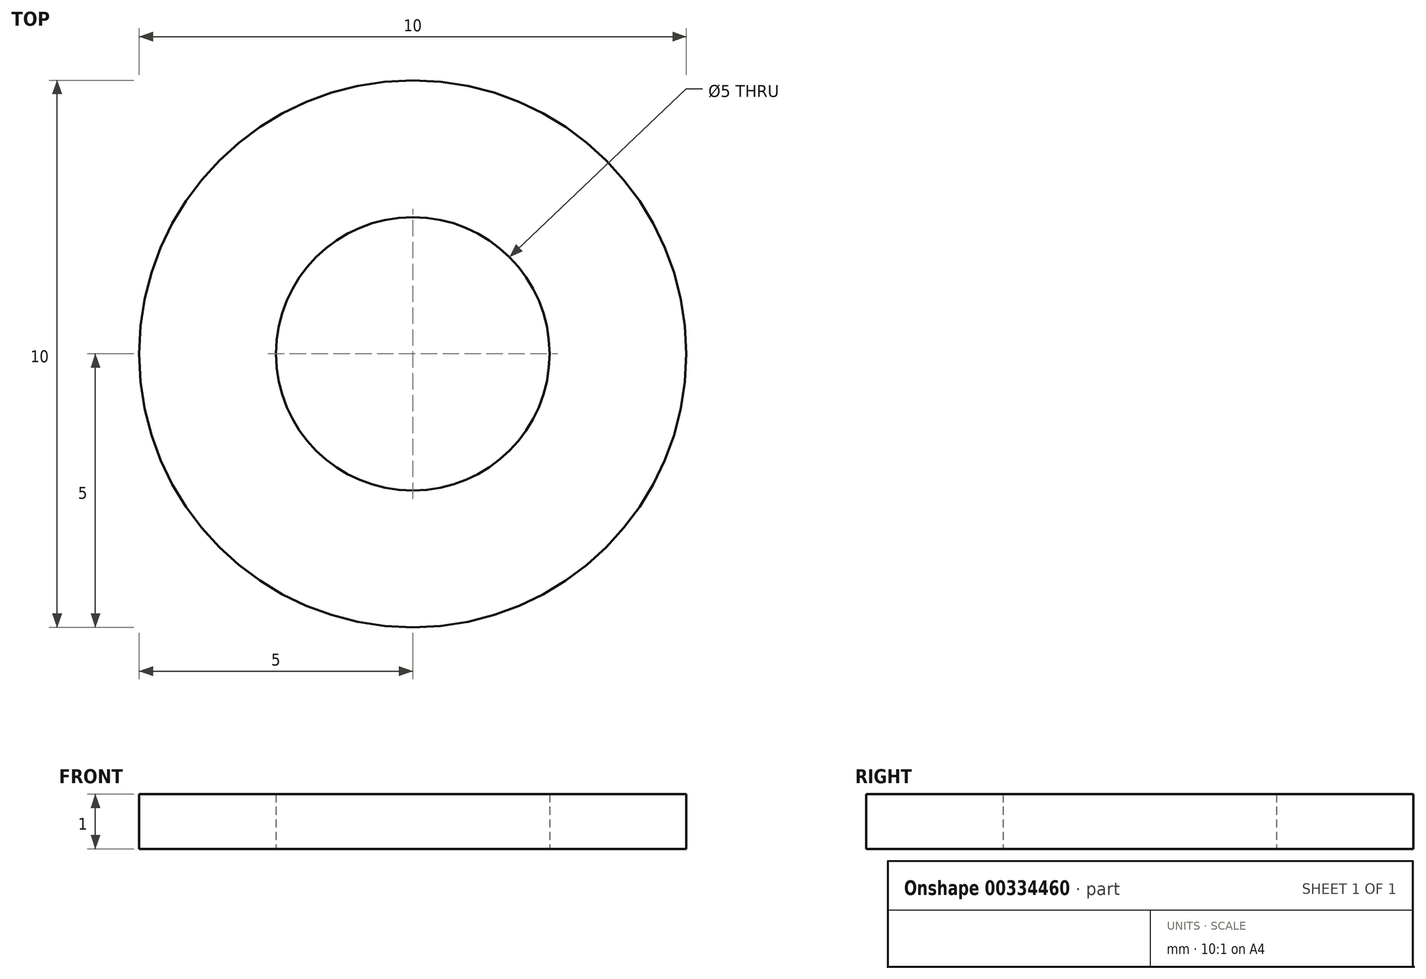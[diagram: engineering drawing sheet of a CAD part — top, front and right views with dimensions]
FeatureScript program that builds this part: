
annotation { "Feature Type Name" : "Feature", "Feature Type Description" : "" }
export const myFeature = defineFeature(function(context is Context, id is Id, definition is map)
    precondition{}
    {
        {
            var Q0;
            Q0=qCreatedBy(makeId("Top.planeOp"),FACE);
            var sketch = newSketch(context, id + "F0", { "sketchPlane" : qUnion([Q0])});
            skCircle(sketch, "E0", {"center": v(0, 0) * mm, "radius": 5 * mm});
            skCircle(sketch, "E1", {"center": v(0, 0) * mm, "radius": 2.5 * mm});
            skSolve(sketch);
        }
        {
            var Q0;
            Q0=makeQuery(id+"F0.imprint","IMPRINT",FACE,{"disambiguationData":[TD([[makeQuery(id+"F0.imprint","IMPRINT",EDGE,{"derivedFrom":sQuery(id+"F0.wireOp",EDGE,"E0")}),1.0]])]});
            extrude(context, id + "F1", {"entities" : qUnion([Q0]), "depth" : 1 * mm});
        }
    });
